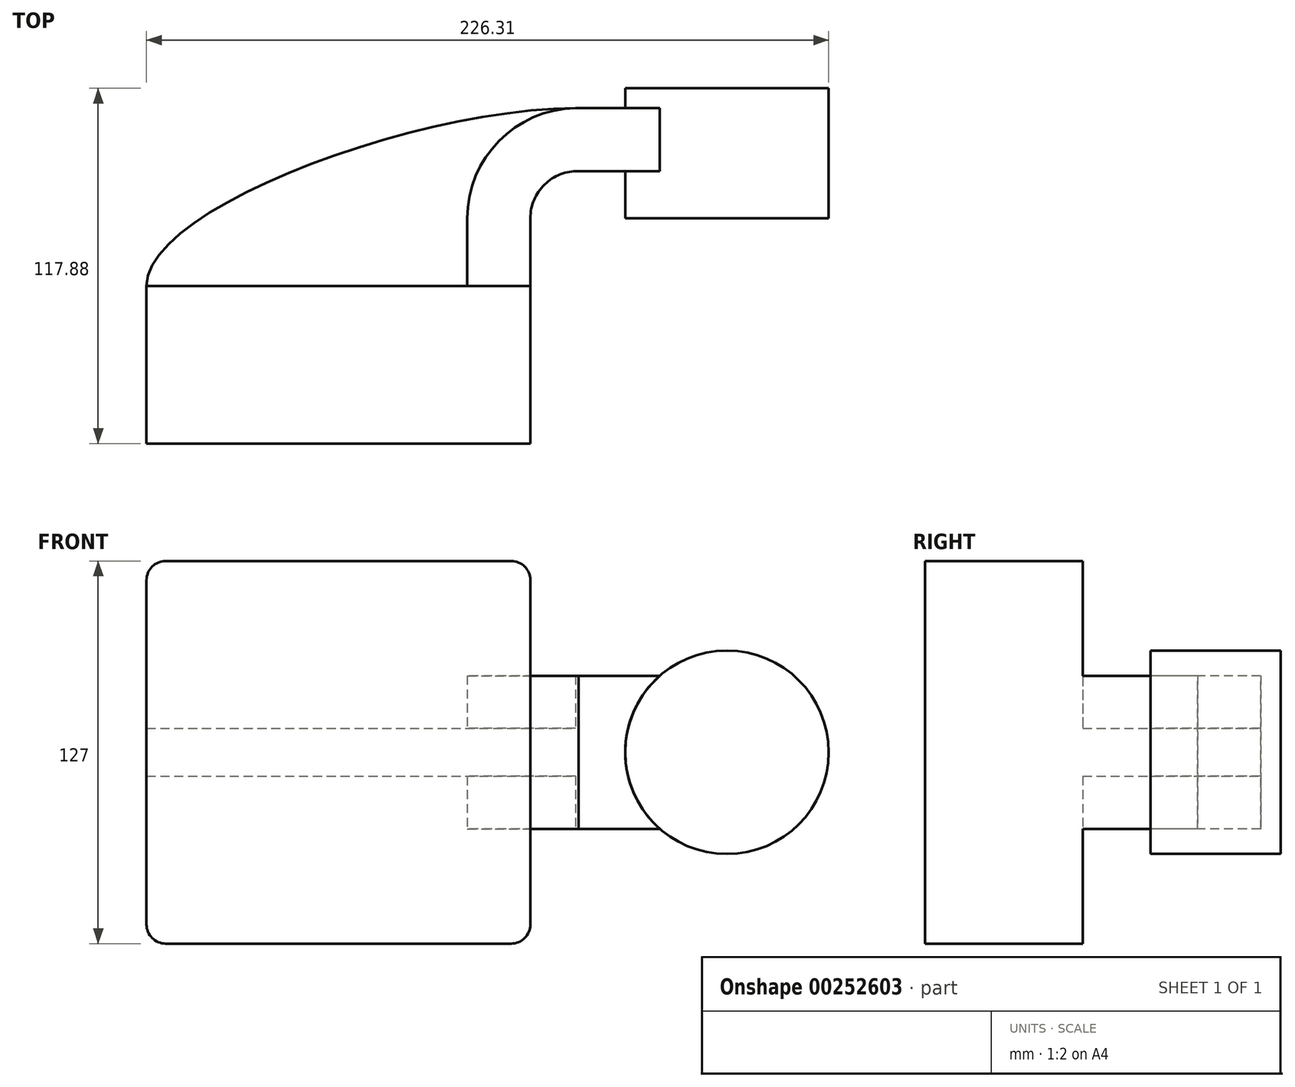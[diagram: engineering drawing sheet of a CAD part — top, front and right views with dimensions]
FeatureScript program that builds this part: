
annotation { "Feature Type Name" : "Feature", "Feature Type Description" : "" }
export const myFeature = defineFeature(function(context is Context, id is Id, definition is map)
    precondition{}
    {
        {
            var Q0;
            Q0=qCreatedBy(makeId("Top.planeOp"),FACE);
            var sketch = newSketch(context, id + "F0", { "sketchPlane" : qUnion([Q0])});
            skLineSegment(sketch, "E0.bottom", {"start": v(-63.52, 28.21) * mm, "end": v(63.82, 28.21) * mm});
            skLineSegment(sketch, "E0.top", {"start": v(-63.52, -24.08) * mm, "end": v(63.82, -24.08) * mm});
            skLineSegment(sketch, "E0.left", {"start": v(-63.52, 28.21) * mm, "end": v(-63.52, -24.08) * mm});
            skLineSegment(sketch, "E0.right", {"start": v(63.82, 28.21) * mm, "end": v(63.82, -24.08) * mm});
            skLineSegment(sketch, "E1.bottom", {"start": v(162.79, 50.67) * mm, "end": v(93.06, 50.67) * mm});
            skLineSegment(sketch, "E1.top", {"start": v(162.79, 93.8) * mm, "end": v(93.06, 93.8) * mm});
            skLineSegment(sketch, "E1.left", {"start": v(162.79, 50.67) * mm, "end": v(162.79, 93.8) * mm});
            skLineSegment(sketch, "E1.right", {"start": v(93.06, 50.67) * mm, "end": v(93.06, 93.8) * mm});
            skPoint(sketch, "E1.middle", {"position": v(127.93, 72.24) * mm});
            skLineSegment(sketch, "E2", {"start": v(63.82, 28.21) * mm, "end": v(63.82, 50.67) * mm});
            skArc(sketch, "E3", {"start": v(63.82, 50.67) * mm, "mid": v(68.53, 61.87) * mm, "end": v(79.83, 66.33) * mm});
            skLineSegment(sketch, "E4", {"start": v(79.83, 66.33) * mm, "end": v(129.03, 66.33) * mm});
            skLineSegment(sketch, "E5.0", {"start": v(80.02, 87.24) * mm, "end": v(129.03, 87.24) * mm});
            skArc(sketch, "E5.1", {"start": v(42.9, 50.67) * mm, "mid": v(53.8, 76.72) * mm, "end": v(80.02, 87.24) * mm});
            skLineSegment(sketch, "E5.2", {"start": v(42.9, 28.21) * mm, "end": v(42.9, 50.67) * mm});
            skLineSegment(sketch, "E6", {"start": v(129.03, 50.67) * mm, "end": v(129.03, 93.8) * mm});
            skFitSpline(sketch, "E7", {"points": [v(-63.52, 28.21) * mm, v(80.02, 87.24) * mm], "startDerivative": vector(-0.72, 77.27) * mm, "endDerivative": vector(161.88, -0.37) * mm});
            skSolve(sketch);
        }
        {
            var Q0;
            Q0=makeQuery(id+"F0.imprint","IMPRINT",FACE,{"disambiguationData":[TD([[makeQuery(id+"F0.imprint","IMPRINT",EDGE,{"derivedFrom":sQuery(id+"F0.wireOp",EDGE,"E0.top")}),1.0]])]});
            extrude(context, id + "F1", {"entities" : qUnion([Q0]), "endBound" : BoundingType.SYMMETRIC, "depth" : 127 * mm});
        }
        {
            var Q0;
            {var subQ1=sQuery(id+"F0.wireOp",EDGE,"E2");Q0=makeQuery(id+"F0.imprint","IMPRINT",FACE,{"disambiguationData":[TD([[makeQuery(id+"F0.imprint","IMPRINT",EDGE,{"derivedFrom":subQ1}),1.0]])]});}
            var Q1;
            {var subQ0=sQuery(id+"F0.wireOp",EDGE,"E4");var subQ1=sQuery(id+"F0.wireOp",EDGE,"E1.right");var subQ2=makeQuery(id+"F0.imprint","INTERSECT",VERTEX,{"derivedFrom":[subQ1,subQ0]});Q1=makeQuery(id+"F0.imprint","IMPRINT",FACE,{"disambiguationData":[TD([[makeQuery(id+"F0.imprint","IMPRINT",EDGE,{"disambiguationData":[TD([[subQ2,-1.0]])],"derivedFrom":subQ1}),-1.0]])]});}
            extrude(context, id + "F2", {"entities" : qUnion([Q0, Q1]), "operationType" : NewBodyOperationType.ADD, "endBound" : BoundingType.SYMMETRIC, "depth" : 50.8 * mm});
        }
        {
            var Q0;
            {var subQ3=sQuery(id+"F0.wireOp",EDGE,"E5.2");Q0=makeQuery(id+"F0.imprint","IMPRINT",FACE,{"disambiguationData":[TD([[makeQuery(id+"F0.imprint","IMPRINT",EDGE,{"derivedFrom":subQ3}),1.0]])]});}
            extrude(context, id + "F3", {"entities" : qUnion([Q0]), "operationType" : NewBodyOperationType.ADD, "endBound" : BoundingType.SYMMETRIC, "depth" : 15.88 * mm});
        }
        {
            var Q0;
            {var subQ0=sQuery(id+"F0.wireOp",EDGE,"E1.left");Q0=makeQuery(id+"F0.imprint","IMPRINT",FACE,{"disambiguationData":[TD([[makeQuery(id+"F0.imprint","IMPRINT",EDGE,{"derivedFrom":subQ0}),1.0]])]});}
            var Q1;
            Q1=sQuery(id+"F0.wireOp",EDGE,"E6");
            revolve(context, id + "F4", {"operationType" : NewBodyOperationType.ADD, "entities" : qUnion([Q0]), "axis" : qUnion([Q1]), "revolveType" : RevolveType.FULL});
        }
        {
            var Q0;
            Q0=makeQuery(id+"F1.opExtrude","CAP_EDGE",EDGE,{"disambiguationData":[OSD([sQuery(id+"F0.wireOp",EDGE,"E0.left")])],"isStart":true});
            var Q1;
            Q1=makeQuery(id+"F1.opExtrude","CAP_EDGE",EDGE,{"disambiguationData":[OSD([sQuery(id+"F0.wireOp",EDGE,"E0.right")])],"isStart":true});
            var Q2;
            Q2=makeQuery(id+"F1.opExtrude","CAP_EDGE",EDGE,{"disambiguationData":[OSD([sQuery(id+"F0.wireOp",EDGE,"E0.left")])],"isStart":false});
            var Q3;
            Q3=makeQuery(id+"F1.opExtrude","CAP_EDGE",EDGE,{"disambiguationData":[OSD([sQuery(id+"F0.wireOp",EDGE,"E0.right")])],"isStart":false});
            fillet(context, id + "F5", {"entities" : qUnion([Q0, Q1, Q2, Q3]), "radius" : 6.35 * mm, "tangentPropagation" : true, "allowEdgeOverflow" : false});
        }
    });
